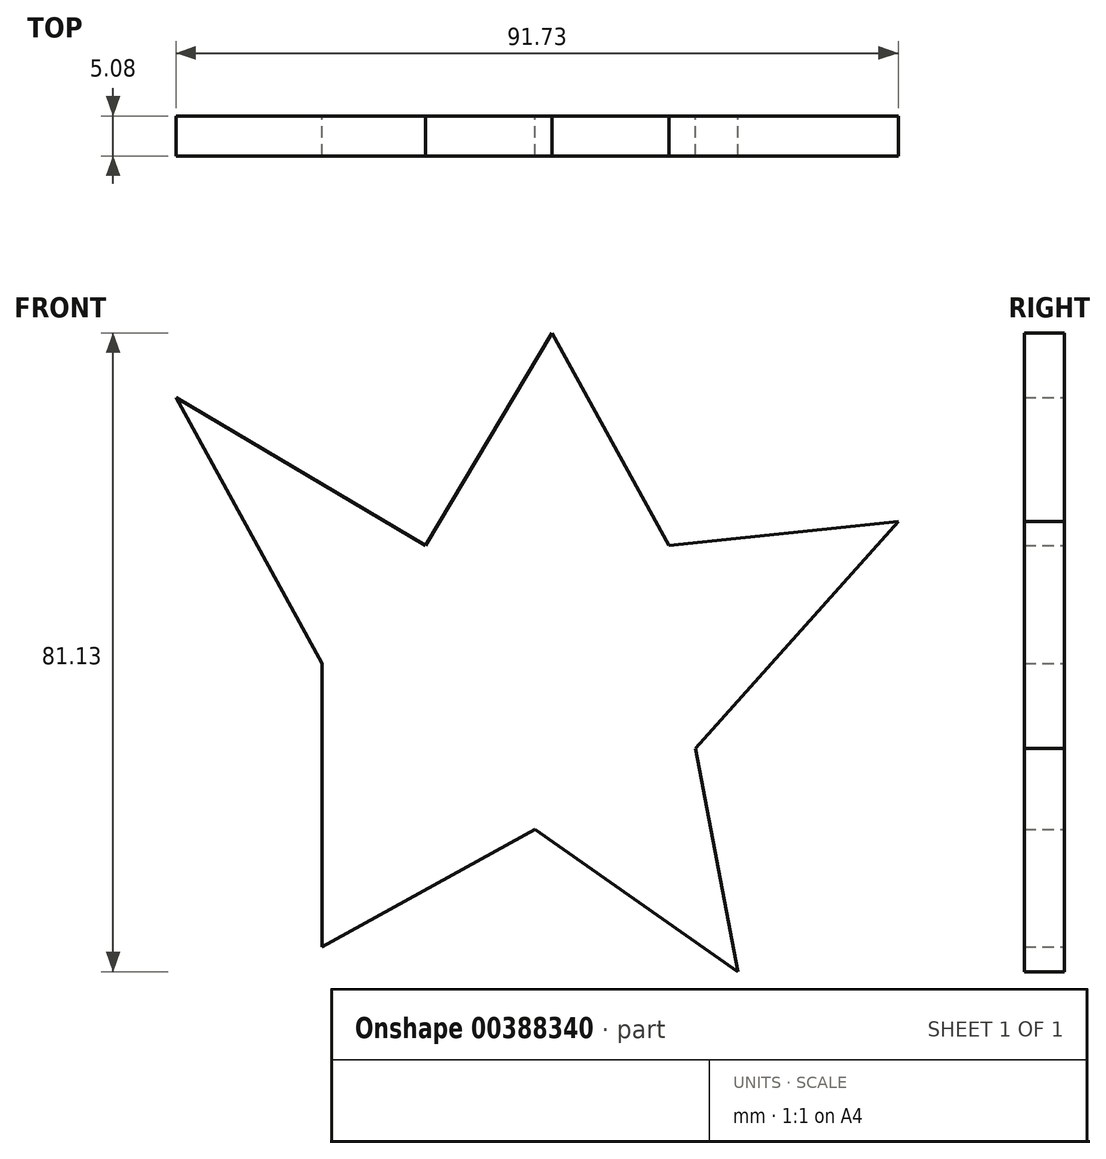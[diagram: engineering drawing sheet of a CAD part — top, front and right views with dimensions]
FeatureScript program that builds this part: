
annotation { "Feature Type Name" : "Feature", "Feature Type Description" : "" }
export const myFeature = defineFeature(function(context is Context, id is Id, definition is map)
    precondition{}
    {
        {
            var Q0;
            Q0=qCreatedBy(makeId("Front.planeOp"),FACE);
            var sketch = newSketch(context, id + "F0", { "sketchPlane" : qUnion([Q0])});
            skLineSegment(sketch, "E0", {"start": v(-23.58, 3.74) * mm, "end": v(-42.13, 37.5) * mm});
            skLineSegment(sketch, "E1", {"start": v(-42.13, 37.5) * mm, "end": v(-10.44, 18.68) * mm});
            skLineSegment(sketch, "E2", {"start": v(-10.44, 18.68) * mm, "end": v(5.6, 45.7) * mm});
            skLineSegment(sketch, "E3", {"start": v(5.6, 45.7) * mm, "end": v(20.45, 18.68) * mm});
            skLineSegment(sketch, "E4", {"start": v(20.45, 18.68) * mm, "end": v(49.6, 21.77) * mm});
            skLineSegment(sketch, "E5", {"start": v(49.6, 21.77) * mm, "end": v(23.84, -7.09) * mm});
            skLineSegment(sketch, "E6", {"start": v(23.84, -7.09) * mm, "end": v(29.25, -35.43) * mm});
            skLineSegment(sketch, "E7", {"start": v(29.25, -35.43) * mm, "end": v(3.48, -17.4) * mm});
            skLineSegment(sketch, "E8", {"start": v(3.48, -17.4) * mm, "end": v(-23.58, -32.26) * mm});
            skLineSegment(sketch, "E9", {"start": v(-23.58, -32.26) * mm, "end": v(-23.58, 3.74) * mm});
            skSolve(sketch);
        }
        {
            var Q0;
            Q0 = qSketchRegion(id + "F0", true);
            extrude(context, id + "F1", {"entities" : qUnion([Q0]), "depth" : 5.08 * mm});
        }
    });
